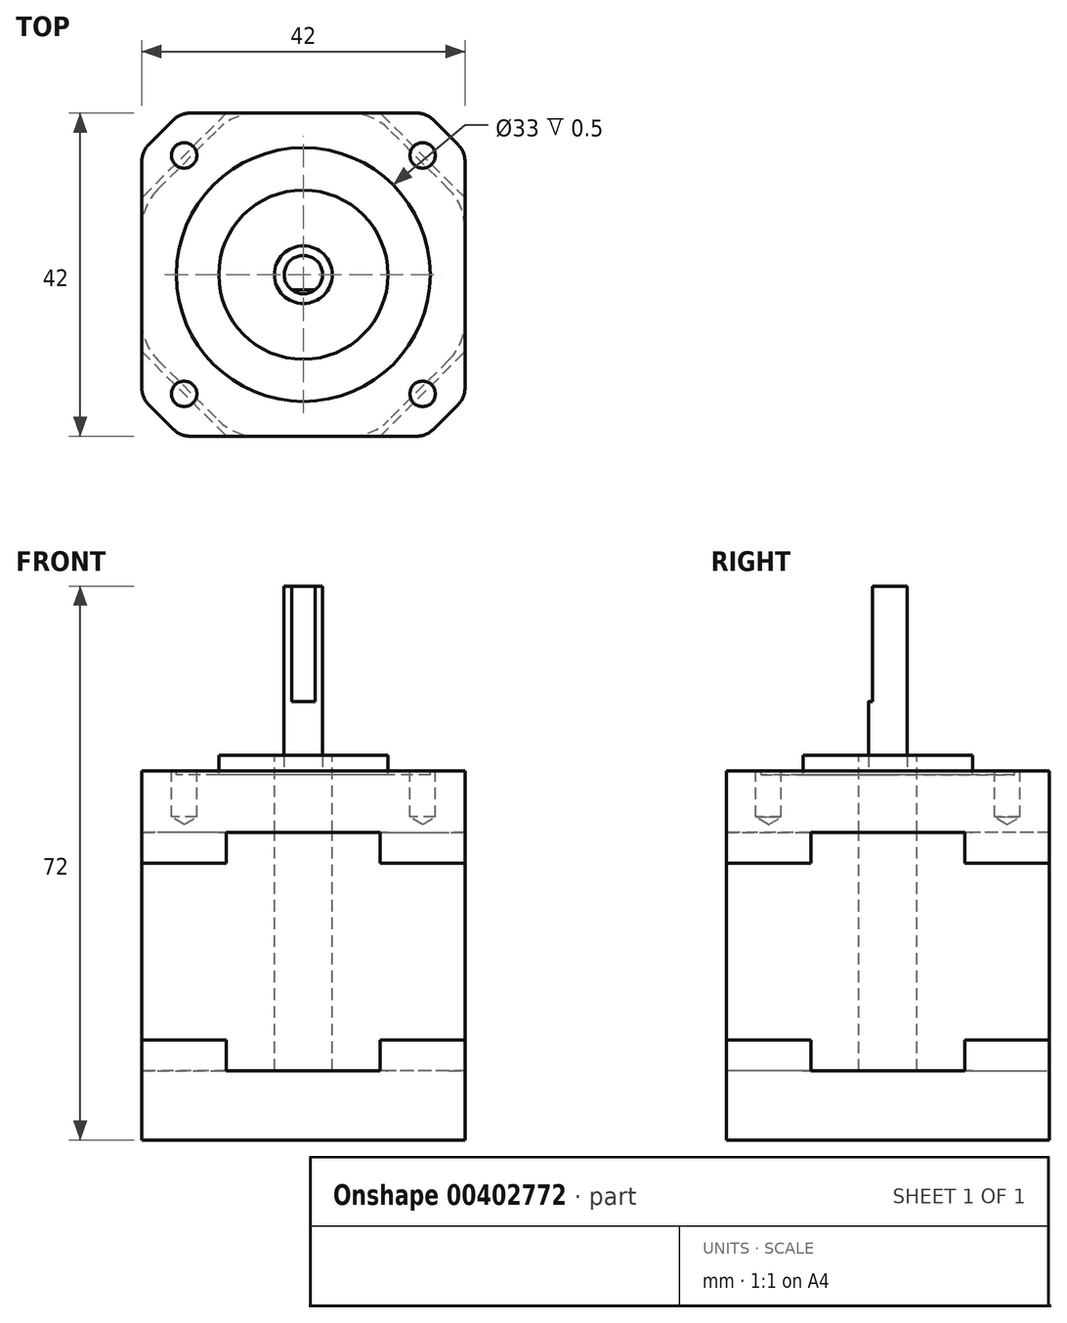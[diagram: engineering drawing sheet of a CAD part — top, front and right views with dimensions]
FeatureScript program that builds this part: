
annotation { "Feature Type Name" : "Feature", "Feature Type Description" : "" }
export const myFeature = defineFeature(function(context is Context, id is Id, definition is map)
    precondition{}
    {
        {
            var Q0;
            Q0=qCreatedBy(makeId("Top.planeOp"),FACE);
            var sketch = newSketch(context, id + "F0", { "sketchPlane" : qUnion([Q0])});
            skLineSegment(sketch, "E0.bottom", {"start": v(21, -21) * mm, "end": v(-21, -21) * mm});
            skLineSegment(sketch, "E0.top", {"start": v(21, 21) * mm, "end": v(-21, 21) * mm});
            skLineSegment(sketch, "E0.left", {"start": v(21, -21) * mm, "end": v(21, 21) * mm});
            skLineSegment(sketch, "E0.right", {"start": v(-21, -21) * mm, "end": v(-21, 21) * mm});
            skPoint(sketch, "E0.middle", {"position": v(0, 0) * mm});
            skCircle(sketch, "E1", {"center": v(0, 0) * mm, "radius": 3.75 * mm});
            skCircle(sketch, "E2", {"center": v(0, 0) * mm, "radius": 11 * mm});
            skCircle(sketch, "E3", {"center": v(0, 0) * mm, "radius": 16.5 * mm});
            skPoint(sketch, "E4", {"position": v(15.5, 15.5) * mm});
            skPoint(sketch, "E5.1.0", {"position": v(-15.5, 15.5) * mm});
            skPoint(sketch, "E5.2.0", {"position": v(-15.5, -15.5) * mm});
            skPoint(sketch, "E5.3.0", {"position": v(15.5, -15.5) * mm});
            skCircle(sketch, "E6", {"center": v(0, 0) * mm, "radius": 2.5 * mm});
            skSolve(sketch);
        }
        {
            var Q0;
            Q0=makeQuery(id+"F0.imprint","IMPRINT",FACE,{"disambiguationData":[TD([[makeQuery(id+"F0.imprint","IMPRINT",EDGE,{"derivedFrom":sQuery(id+"F0.wireOp",EDGE,"E0.bottom")}),-1.0]])]});
            var Q1;
            Q1=makeQuery(id+"F0.imprint","IMPRINT",FACE,{"disambiguationData":[TD([[makeQuery(id+"F0.imprint","IMPRINT",EDGE,{"derivedFrom":sQuery(id+"F0.wireOp",EDGE,"E2")}),-1.0]])]});
            var Q2;
            Q2=makeQuery(id+"F0.imprint","IMPRINT",FACE,{"disambiguationData":[TD([[makeQuery(id+"F0.imprint","IMPRINT",EDGE,{"derivedFrom":sQuery(id+"F0.wireOp",EDGE,"E1")}),-1.0]])]});
            extrude(context, id + "F1", {"entities" : qUnion([Q0, Q1, Q2]), "oppositeDirection" : true, "depth" : 8 * mm});
        }
        {
            var Q0;
            Q0=makeQuery(id+"F0.imprint","IMPRINT",FACE,{"disambiguationData":[TD([[makeQuery(id+"F0.imprint","IMPRINT",EDGE,{"derivedFrom":sQuery(id+"F0.wireOp",EDGE,"E2")}),-1.0]])]});
            extrude(context, id + "F2", {"entities" : qUnion([Q0]), "operationType" : NewBodyOperationType.REMOVE, "oppositeDirection" : true, "depth" : .5 * mm});
        }
        {
            var Q0;
            Q0=makeQuery(id+"F0.imprint","IMPRINT",FACE,{"disambiguationData":[TD([[makeQuery(id+"F0.imprint","IMPRINT",EDGE,{"derivedFrom":sQuery(id+"F0.wireOp",EDGE,"E1")}),-1.0]])]});
            extrude(context, id + "F3", {"entities" : qUnion([Q0]), "operationType" : NewBodyOperationType.ADD, "depth" : 2 * mm});
        }
        {
            var Q0;
            Q0=makeQuery(id+"F1.opExtrude","SWEPT_EDGE",EDGE,{"disambiguationData":[OSD([sQuery(id+"F0.wireOp",EDGE,"E0.bottom"),sQuery(id+"F0.wireOp",EDGE,"E0.left")])]});
            var Q1;
            Q1=makeQuery(id+"F1.opExtrude","SWEPT_EDGE",EDGE,{"disambiguationData":[OSD([sQuery(id+"F0.wireOp",EDGE,"E0.top"),sQuery(id+"F0.wireOp",EDGE,"E0.left")])]});
            var Q2;
            Q2=makeQuery(id+"F1.opExtrude","SWEPT_EDGE",EDGE,{"disambiguationData":[OSD([sQuery(id+"F0.wireOp",EDGE,"E0.bottom"),sQuery(id+"F0.wireOp",EDGE,"E0.right")])]});
            var Q3;
            Q3=makeQuery(id+"F1.opExtrude","SWEPT_EDGE",EDGE,{"disambiguationData":[OSD([sQuery(id+"F0.wireOp",EDGE,"E0.top"),sQuery(id+"F0.wireOp",EDGE,"E0.right")])]});
            chamfer(context, id + "F4", {"entities" : qUnion([Q0, Q1, Q2, Q3]), "width" : 5 * mm, "tangentPropagation" : true});
        }
        {
            var Q0;
            Q0=makeQuery(id+"F1.opExtrude","CAP_FACE",FACE,{"disambiguationData":[OSD([sQuery(id+"F0.wireOp",EDGE,"E0.bottom"),sQuery(id+"F0.wireOp",EDGE,"E0.top"),sQuery(id+"F0.wireOp",EDGE,"E0.left"),sQuery(id+"F0.wireOp",EDGE,"E0.right"),sQuery(id+"F0.wireOp",EDGE,"E1")])],"isStart":false});
            var sketch = newSketch(context, id + "F5", { "sketchPlane" : qUnion([Q0])});
            skLineSegment(sketch, "E7.bottom", {"start": v(-21, -21) * mm, "end": v(21, -21) * mm});
            skLineSegment(sketch, "E7.top", {"start": v(-21, 21) * mm, "end": v(21, 21) * mm});
            skLineSegment(sketch, "E7.left", {"start": v(-21, -21) * mm, "end": v(-21, 21) * mm});
            skLineSegment(sketch, "E7.right", {"start": v(21, -21) * mm, "end": v(21, 21) * mm});
            skPoint(sketch, "E7.middle", {"position": v(0, 0) * mm});
            skSolve(sketch);
        }
        {
            var Q0;
            {var subQ1=sQuery(id+"F0.wireOp",EDGE,"E1");Q0=makeQuery(id+"F5.imprint","IMPRINT",FACE,{"disambiguationData":[TD([[makeQuery(id+"F5.imprint","IMPRINT",EDGE,{"derivedFrom":makeQuery(id+"F1.opExtrude","CAP_EDGE",EDGE,{"disambiguationData":[OSD([subQ1])],"isStart":false})}),1.0]])]});}
            var Q1;
            {var subQ1=sQuery(id+"F0.wireOp",EDGE,"E0.left");var subQ2=sQuery(id+"F0.wireOp",EDGE,"E0.top");var subQ3=makeQuery(id+"F4.opChamfer","BLEND_EDGE",EDGE,{"blendedFrom":[makeQuery(id+"F1.opExtrude","SWEPT_EDGE",EDGE,{"disambiguationData":[OSD([subQ2,subQ1])]}),makeQuery(id+"F1.opExtrude","CAP_FACE",FACE,{"disambiguationData":[OSD([sQuery(id+"F0.wireOp",EDGE,"E0.bottom"),subQ2,subQ1,sQuery(id+"F0.wireOp",EDGE,"E0.right"),sQuery(id+"F0.wireOp",EDGE,"E1")])],"isStart":false})],"blendedInto":[makeQuery(id+"F1.opExtrude","CAP_FACE",FACE,{"disambiguationData":[OSD([sQuery(id+"F0.wireOp",EDGE,"E0.bottom"),subQ2,subQ1,sQuery(id+"F0.wireOp",EDGE,"E0.right"),sQuery(id+"F0.wireOp",EDGE,"E1")])],"isStart":false})]});Q1=makeQuery(id+"F5.imprint","IMPRINT",FACE,{"disambiguationData":[TD([[makeQuery(id+"F5.imprint","IMPRINT",EDGE,{"derivedFrom":subQ3}),-1.0]])]});}
            var Q2;
            {var subQ1=sQuery(id+"F0.wireOp",EDGE,"E0.right");var subQ2=sQuery(id+"F0.wireOp",EDGE,"E0.top");var subQ3=makeQuery(id+"F4.opChamfer","BLEND_EDGE",EDGE,{"blendedFrom":[makeQuery(id+"F1.opExtrude","SWEPT_EDGE",EDGE,{"disambiguationData":[OSD([subQ2,subQ1])]}),makeQuery(id+"F1.opExtrude","CAP_FACE",FACE,{"disambiguationData":[OSD([sQuery(id+"F0.wireOp",EDGE,"E0.bottom"),subQ2,sQuery(id+"F0.wireOp",EDGE,"E0.left"),subQ1,sQuery(id+"F0.wireOp",EDGE,"E1")])],"isStart":false})],"blendedInto":[makeQuery(id+"F1.opExtrude","CAP_FACE",FACE,{"disambiguationData":[OSD([sQuery(id+"F0.wireOp",EDGE,"E0.bottom"),subQ2,sQuery(id+"F0.wireOp",EDGE,"E0.left"),subQ1,sQuery(id+"F0.wireOp",EDGE,"E1")])],"isStart":false})]});Q2=makeQuery(id+"F5.imprint","IMPRINT",FACE,{"disambiguationData":[TD([[makeQuery(id+"F5.imprint","IMPRINT",EDGE,{"derivedFrom":subQ3}),-1.0]])]});}
            var Q3;
            {var subQ1=sQuery(id+"F0.wireOp",EDGE,"E0.right");var subQ2=sQuery(id+"F0.wireOp",EDGE,"E0.bottom");var subQ3=makeQuery(id+"F4.opChamfer","BLEND_EDGE",EDGE,{"blendedFrom":[makeQuery(id+"F1.opExtrude","SWEPT_EDGE",EDGE,{"disambiguationData":[OSD([subQ2,subQ1])]}),makeQuery(id+"F1.opExtrude","CAP_FACE",FACE,{"disambiguationData":[OSD([subQ2,sQuery(id+"F0.wireOp",EDGE,"E0.top"),sQuery(id+"F0.wireOp",EDGE,"E0.left"),subQ1,sQuery(id+"F0.wireOp",EDGE,"E1")])],"isStart":false})],"blendedInto":[makeQuery(id+"F1.opExtrude","CAP_FACE",FACE,{"disambiguationData":[OSD([subQ2,sQuery(id+"F0.wireOp",EDGE,"E0.top"),sQuery(id+"F0.wireOp",EDGE,"E0.left"),subQ1,sQuery(id+"F0.wireOp",EDGE,"E1")])],"isStart":false})]});Q3=makeQuery(id+"F5.imprint","IMPRINT",FACE,{"disambiguationData":[TD([[makeQuery(id+"F5.imprint","IMPRINT",EDGE,{"derivedFrom":subQ3}),-1.0]])]});}
            var Q4;
            {var subQ1=sQuery(id+"F0.wireOp",EDGE,"E0.left");var subQ2=sQuery(id+"F0.wireOp",EDGE,"E0.bottom");var subQ3=makeQuery(id+"F4.opChamfer","BLEND_EDGE",EDGE,{"blendedFrom":[makeQuery(id+"F1.opExtrude","SWEPT_EDGE",EDGE,{"disambiguationData":[OSD([subQ2,subQ1])]}),makeQuery(id+"F1.opExtrude","CAP_FACE",FACE,{"disambiguationData":[OSD([subQ2,sQuery(id+"F0.wireOp",EDGE,"E0.top"),subQ1,sQuery(id+"F0.wireOp",EDGE,"E0.right"),sQuery(id+"F0.wireOp",EDGE,"E1")])],"isStart":false})],"blendedInto":[makeQuery(id+"F1.opExtrude","CAP_FACE",FACE,{"disambiguationData":[OSD([subQ2,sQuery(id+"F0.wireOp",EDGE,"E0.top"),subQ1,sQuery(id+"F0.wireOp",EDGE,"E0.right"),sQuery(id+"F0.wireOp",EDGE,"E1")])],"isStart":false})]});Q4=makeQuery(id+"F5.imprint","IMPRINT",FACE,{"disambiguationData":[TD([[makeQuery(id+"F5.imprint","IMPRINT",EDGE,{"derivedFrom":subQ3}),-1.0]])]});}
            extrude(context, id + "F6", {"entities" : qUnion([Q0, Q1, Q2, Q3, Q4]), "depth" : 31 * mm});
        }
        {
            var Q0;
            Q0=makeQuery(id+"F6.opExtrude","SWEPT_EDGE",EDGE,{"disambiguationData":[OSD([sQuery(id+"F5.wireOp",EDGE,"E7.bottom"),sQuery(id+"F5.wireOp",EDGE,"E7.left")])]});
            var Q1;
            Q1=makeQuery(id+"F6.opExtrude","SWEPT_EDGE",EDGE,{"disambiguationData":[OSD([sQuery(id+"F5.wireOp",EDGE,"E7.bottom"),sQuery(id+"F5.wireOp",EDGE,"E7.right")])]});
            var Q2;
            Q2=makeQuery(id+"F6.opExtrude","SWEPT_EDGE",EDGE,{"disambiguationData":[OSD([sQuery(id+"F5.wireOp",EDGE,"E7.top"),sQuery(id+"F5.wireOp",EDGE,"E7.left")])]});
            var Q3;
            Q3=makeQuery(id+"F6.opExtrude","SWEPT_EDGE",EDGE,{"disambiguationData":[OSD([sQuery(id+"F5.wireOp",EDGE,"E7.top"),sQuery(id+"F5.wireOp",EDGE,"E7.right")])]});
            chamfer(context, id + "F7", {"entities" : qUnion([Q0, Q1, Q2, Q3]), "width" : 12 * mm, "tangentPropagation" : true});
        }
        {
            var Q0;
            Q0=makeQuery(id+"F6.opExtrude","CAP_FACE",FACE,{"disambiguationData":[OSD([sQuery(id+"F0.wireOp",EDGE,"E1"),sQuery(id+"F5.wireOp",EDGE,"E7.bottom"),sQuery(id+"F5.wireOp",EDGE,"E7.top"),sQuery(id+"F5.wireOp",EDGE,"E7.left"),sQuery(id+"F5.wireOp",EDGE,"E7.right")])],"isStart":false});
            var sketch = newSketch(context, id + "F8", { "sketchPlane" : qUnion([Q0])});
            skLineSegment(sketch, "E8.bottom", {"start": v(-21, -21) * mm, "end": v(21, -21) * mm});
            skLineSegment(sketch, "E8.top", {"start": v(-21, 21) * mm, "end": v(21, 21) * mm});
            skLineSegment(sketch, "E8.left", {"start": v(-21, -21) * mm, "end": v(-21, 21) * mm});
            skLineSegment(sketch, "E8.right", {"start": v(21, -21) * mm, "end": v(21, 21) * mm});
            skPoint(sketch, "E8.middle", {"position": v(0, 0) * mm});
            skSolve(sketch);
        }
        {
            var Q0;
            {var subQ1=sQuery(id+"F5.wireOp",EDGE,"E7.right");var subQ2=sQuery(id+"F5.wireOp",EDGE,"E7.bottom");var subQ3=makeQuery(id+"F7.opChamfer","BLEND_EDGE",EDGE,{"blendedFrom":[makeQuery(id+"F6.opExtrude","SWEPT_EDGE",EDGE,{"disambiguationData":[OSD([subQ2,subQ1])]}),makeQuery(id+"F6.opExtrude","CAP_FACE",FACE,{"disambiguationData":[OSD([sQuery(id+"F0.wireOp",EDGE,"E1"),subQ2,sQuery(id+"F5.wireOp",EDGE,"E7.top"),sQuery(id+"F5.wireOp",EDGE,"E7.left"),subQ1])],"isStart":false})],"blendedInto":[makeQuery(id+"F6.opExtrude","CAP_FACE",FACE,{"disambiguationData":[OSD([sQuery(id+"F0.wireOp",EDGE,"E1"),subQ2,sQuery(id+"F5.wireOp",EDGE,"E7.top"),sQuery(id+"F5.wireOp",EDGE,"E7.left"),subQ1])],"isStart":false})]});Q0=makeQuery(id+"F8.imprint","IMPRINT",FACE,{"disambiguationData":[TD([[makeQuery(id+"F8.imprint","IMPRINT",EDGE,{"derivedFrom":subQ3}),-1.0]])]});}
            var Q1;
            {var subQ1=sQuery(id+"F5.wireOp",EDGE,"E7.right");var subQ2=sQuery(id+"F5.wireOp",EDGE,"E7.top");var subQ3=makeQuery(id+"F7.opChamfer","BLEND_EDGE",EDGE,{"blendedFrom":[makeQuery(id+"F6.opExtrude","SWEPT_EDGE",EDGE,{"disambiguationData":[OSD([subQ2,subQ1])]}),makeQuery(id+"F6.opExtrude","CAP_FACE",FACE,{"disambiguationData":[OSD([sQuery(id+"F0.wireOp",EDGE,"E1"),sQuery(id+"F5.wireOp",EDGE,"E7.bottom"),subQ2,sQuery(id+"F5.wireOp",EDGE,"E7.left"),subQ1])],"isStart":false})],"blendedInto":[makeQuery(id+"F6.opExtrude","CAP_FACE",FACE,{"disambiguationData":[OSD([sQuery(id+"F0.wireOp",EDGE,"E1"),sQuery(id+"F5.wireOp",EDGE,"E7.bottom"),subQ2,sQuery(id+"F5.wireOp",EDGE,"E7.left"),subQ1])],"isStart":false})]});Q1=makeQuery(id+"F8.imprint","IMPRINT",FACE,{"disambiguationData":[TD([[makeQuery(id+"F8.imprint","IMPRINT",EDGE,{"derivedFrom":subQ3}),-1.0]])]});}
            var Q2;
            {var subQ1=sQuery(id+"F5.wireOp",EDGE,"E7.left");var subQ2=sQuery(id+"F5.wireOp",EDGE,"E7.top");var subQ3=makeQuery(id+"F7.opChamfer","BLEND_EDGE",EDGE,{"blendedFrom":[makeQuery(id+"F6.opExtrude","SWEPT_EDGE",EDGE,{"disambiguationData":[OSD([subQ2,subQ1])]}),makeQuery(id+"F6.opExtrude","CAP_FACE",FACE,{"disambiguationData":[OSD([sQuery(id+"F0.wireOp",EDGE,"E1"),sQuery(id+"F5.wireOp",EDGE,"E7.bottom"),subQ2,subQ1,sQuery(id+"F5.wireOp",EDGE,"E7.right")])],"isStart":false})],"blendedInto":[makeQuery(id+"F6.opExtrude","CAP_FACE",FACE,{"disambiguationData":[OSD([sQuery(id+"F0.wireOp",EDGE,"E1"),sQuery(id+"F5.wireOp",EDGE,"E7.bottom"),subQ2,subQ1,sQuery(id+"F5.wireOp",EDGE,"E7.right")])],"isStart":false})]});Q2=makeQuery(id+"F8.imprint","IMPRINT",FACE,{"disambiguationData":[TD([[makeQuery(id+"F8.imprint","IMPRINT",EDGE,{"derivedFrom":subQ3}),-1.0]])]});}
            var Q3;
            {var subQ1=sQuery(id+"F5.wireOp",EDGE,"E7.left");var subQ2=sQuery(id+"F5.wireOp",EDGE,"E7.bottom");var subQ3=makeQuery(id+"F7.opChamfer","BLEND_EDGE",EDGE,{"blendedFrom":[makeQuery(id+"F6.opExtrude","SWEPT_EDGE",EDGE,{"disambiguationData":[OSD([subQ2,subQ1])]}),makeQuery(id+"F6.opExtrude","CAP_FACE",FACE,{"disambiguationData":[OSD([sQuery(id+"F0.wireOp",EDGE,"E1"),subQ2,sQuery(id+"F5.wireOp",EDGE,"E7.top"),subQ1,sQuery(id+"F5.wireOp",EDGE,"E7.right")])],"isStart":false})],"blendedInto":[makeQuery(id+"F6.opExtrude","CAP_FACE",FACE,{"disambiguationData":[OSD([sQuery(id+"F0.wireOp",EDGE,"E1"),subQ2,sQuery(id+"F5.wireOp",EDGE,"E7.top"),subQ1,sQuery(id+"F5.wireOp",EDGE,"E7.right")])],"isStart":false})]});Q3=makeQuery(id+"F8.imprint","IMPRINT",FACE,{"disambiguationData":[TD([[makeQuery(id+"F8.imprint","IMPRINT",EDGE,{"derivedFrom":subQ3}),-1.0]])]});}
            var Q4;
            {var subQ5=sQuery(id+"F0.wireOp",EDGE,"E1");Q4=makeQuery(id+"F8.imprint","IMPRINT",FACE,{"disambiguationData":[TD([[makeQuery(id+"F8.imprint","IMPRINT",EDGE,{"derivedFrom":makeQuery(id+"F6.opExtrude","CAP_EDGE",EDGE,{"disambiguationData":[OSD([subQ5])],"isStart":false})}),1.0]])]});}
            var Q5;
            Q5=makeQuery(id+"F8.imprint","IMPRINT",FACE,{"disambiguationData":[TD([[makeQuery(id+"F8.imprint","IMPRINT",EDGE,{"derivedFrom":makeQuery(id+"F6.opExtrude","CAP_EDGE",EDGE,{"disambiguationData":[OSD([sQuery(id+"F0.wireOp",EDGE,"E1")])],"isStart":false})}),-1.0]])]});
            extrude(context, id + "F9", {"entities" : qUnion([Q0, Q1, Q2, Q3, Q4, Q5]), "depth" : 9 * mm});
        }
        {
            var Q0;
            Q0=makeQuery(id+"F9.opExtrude","SWEPT_EDGE",EDGE,{"disambiguationData":[OSD([sQuery(id+"F8.wireOp",EDGE,"E8.top"),sQuery(id+"F8.wireOp",EDGE,"E8.left")])]});
            var Q1;
            Q1=makeQuery(id+"F9.opExtrude","SWEPT_EDGE",EDGE,{"disambiguationData":[OSD([sQuery(id+"F8.wireOp",EDGE,"E8.bottom"),sQuery(id+"F8.wireOp",EDGE,"E8.left")])]});
            var Q2;
            Q2=makeQuery(id+"F9.opExtrude","SWEPT_EDGE",EDGE,{"disambiguationData":[OSD([sQuery(id+"F8.wireOp",EDGE,"E8.top"),sQuery(id+"F8.wireOp",EDGE,"E8.right")])]});
            var Q3;
            Q3=makeQuery(id+"F9.opExtrude","SWEPT_EDGE",EDGE,{"disambiguationData":[OSD([sQuery(id+"F8.wireOp",EDGE,"E8.bottom"),sQuery(id+"F8.wireOp",EDGE,"E8.right")])]});
            chamfer(context, id + "F10", {"entities" : qUnion([Q0, Q1, Q2, Q3]), "width" : 5 * mm, "tangentPropagation" : true});
        }
        {
            var Q0;
            Q0=sQuery(id+"F0.wireOp",VERTEX,"E5.1.0");
            var Q1;
            Q1=sQuery(id+"F0.wireOp",VERTEX,"E4");
            var Q2;
            Q2=sQuery(id+"F0.wireOp",VERTEX,"E5.3.0");
            var Q3;
            Q3=sQuery(id+"F0.wireOp",VERTEX,"E5.2.0");
            var Q4;
            Q4=makeQuery(id+"F1.opExtrude","SWEPT_BODY",BODY,{"disambiguationData":[OSD([sQuery(id+"F0.wireOp",EDGE,"E0.bottom"),sQuery(id+"F0.wireOp",EDGE,"E0.top"),sQuery(id+"F0.wireOp",EDGE,"E0.left"),sQuery(id+"F0.wireOp",EDGE,"E0.right"),sQuery(id+"F0.wireOp",EDGE,"E1")])]});
            hole(context, id + "F11", {"style" : HoleStyle.SIMPLE, "endStyle" : HoleEndStyle.BLIND, "standardTappedOrClearance" : lookupTablePath({ "fit" : "Normal", "standard" : "ISO", "engagement" : "75%", "pitch" : "0.5 mm", "size" : "M3", "type" : "Clearance & tapped" }), "standardBlindInLast" : lookupTablePath({ "standard" : "ISO", "fit" : "Standard", "engagement" : "75%", "pitch" : "0.5 mm", "size" : "M3", "type" : "Clearance & tapped" }), "holeDiameter" : 3.3 * mm, "showTappedDepth" : true, "holeDepth" : 6 * mm, "isTappedThrough" : true, "tappedDepth" : 4.5 * mm, "tapClearance" : 3, "locations" : qUnion([Q0, Q1, Q2, Q3]), "scope" : qUnion([Q4])});
        }
        {
            var Q0;
            Q0=makeQuery(id+"F9.opExtrude","CAP_FACE",FACE,{"disambiguationData":[OSD([sQuery(id+"F0.wireOp",EDGE,"E1"),sQuery(id+"F8.wireOp",EDGE,"E8.bottom"),sQuery(id+"F8.wireOp",EDGE,"E8.top"),sQuery(id+"F8.wireOp",EDGE,"E8.left"),sQuery(id+"F8.wireOp",EDGE,"E8.right")])],"isStart":true});
            var sketch = newSketch(context, id + "F12", { "sketchPlane" : qUnion([Q0])});
            skLineSegment(sketch, "E9", {"start": v(-21, 16) * mm, "end": v(-16, 21) * mm});
            skLineSegment(sketch, "E10", {"start": v(-16, 21) * mm, "end": v(-10, 21) * mm});
            skLineSegment(sketch, "E11", {"start": v(-10, 21) * mm, "end": v(-21, 10) * mm});
            skLineSegment(sketch, "E12", {"start": v(-21, 10) * mm, "end": v(-21, 16) * mm});
            skLineSegment(sketch, "E13.1.0", {"start": v(-21, -10) * mm, "end": v(-10, -21) * mm});
            skLineSegment(sketch, "E13.1.1", {"start": v(-16, -21) * mm, "end": v(-21, -16) * mm});
            skLineSegment(sketch, "E13.1.2", {"start": v(-21, -16) * mm, "end": v(-21, -10) * mm});
            skLineSegment(sketch, "E13.1.3", {"start": v(-10, -21) * mm, "end": v(-16, -21) * mm});
            skLineSegment(sketch, "E13.2.0", {"start": v(10, -21) * mm, "end": v(21, -10) * mm});
            skLineSegment(sketch, "E13.2.1", {"start": v(21, -16) * mm, "end": v(16, -21) * mm});
            skLineSegment(sketch, "E13.2.2", {"start": v(16, -21) * mm, "end": v(10, -21) * mm});
            skLineSegment(sketch, "E13.2.3", {"start": v(21, -10) * mm, "end": v(21, -16) * mm});
            skLineSegment(sketch, "E13.3.0", {"start": v(21, 10) * mm, "end": v(10, 21) * mm});
            skLineSegment(sketch, "E13.3.1", {"start": v(16, 21) * mm, "end": v(21, 16) * mm});
            skLineSegment(sketch, "E13.3.2", {"start": v(21, 16) * mm, "end": v(21, 10) * mm});
            skLineSegment(sketch, "E13.3.3", {"start": v(10, 21) * mm, "end": v(16, 21) * mm});
            skPoint(sketch, "E13.center", {"position": v(0, 0) * mm});
            skSolve(sketch);
        }
        {
            var Q0;
            Q0=makeQuery(id+"F12.imprint","IMPRINT",FACE,{"disambiguationData":[TD([[makeQuery(id+"F12.imprint","IMPRINT",EDGE,{"derivedFrom":sQuery(id+"F12.wireOp",EDGE,"E9")}),1.0]])]});
            var Q1;
            Q1=makeQuery(id+"F12.imprint","IMPRINT",FACE,{"disambiguationData":[TD([[makeQuery(id+"F12.imprint","IMPRINT",EDGE,{"derivedFrom":sQuery(id+"F12.wireOp",EDGE,"E13.1.0")}),-1.0]])]});
            var Q2;
            Q2=makeQuery(id+"F12.imprint","IMPRINT",FACE,{"disambiguationData":[TD([[makeQuery(id+"F12.imprint","IMPRINT",EDGE,{"derivedFrom":sQuery(id+"F12.wireOp",EDGE,"E13.2.0")}),-1.0]])]});
            var Q3;
            Q3=makeQuery(id+"F12.imprint","IMPRINT",FACE,{"disambiguationData":[TD([[makeQuery(id+"F12.imprint","IMPRINT",EDGE,{"derivedFrom":sQuery(id+"F12.wireOp",EDGE,"E13.3.0")}),-1.0]])]});
            extrude(context, id + "F13", {"entities" : qUnion([Q0, Q1, Q2, Q3]), "operationType" : NewBodyOperationType.ADD, "depth" : 4 * mm});
        }
        {
            var Q0;
            Q0=makeQuery(id+"F1.opExtrude","CAP_FACE",FACE,{"disambiguationData":[OSD([sQuery(id+"F0.wireOp",EDGE,"E0.bottom"),sQuery(id+"F0.wireOp",EDGE,"E0.top"),sQuery(id+"F0.wireOp",EDGE,"E0.left"),sQuery(id+"F0.wireOp",EDGE,"E0.right"),sQuery(id+"F0.wireOp",EDGE,"E1")])],"isStart":false});
            var sketch = newSketch(context, id + "F14", { "sketchPlane" : qUnion([Q0])});
            skLineSegment(sketch, "E14", {"start": v(16, 21) * mm, "end": v(21, 16) * mm});
            skLineSegment(sketch, "E15", {"start": v(21, 16) * mm, "end": v(21, 10) * mm});
            skLineSegment(sketch, "E16", {"start": v(21, 10) * mm, "end": v(10, 21) * mm});
            skLineSegment(sketch, "E17", {"start": v(10, 21) * mm, "end": v(16, 21) * mm});
            skLineSegment(sketch, "E18.1.0", {"start": v(-10, 21) * mm, "end": v(-21, 10) * mm});
            skLineSegment(sketch, "E18.1.1", {"start": v(-21, 10) * mm, "end": v(-21, 16) * mm});
            skLineSegment(sketch, "E18.1.2", {"start": v(-16, 21) * mm, "end": v(-10, 21) * mm});
            skLineSegment(sketch, "E18.1.3", {"start": v(-21, 16) * mm, "end": v(-16, 21) * mm});
            skLineSegment(sketch, "E18.2.0", {"start": v(-21, -10) * mm, "end": v(-10, -21) * mm});
            skLineSegment(sketch, "E18.2.1", {"start": v(-10, -21) * mm, "end": v(-16, -21) * mm});
            skLineSegment(sketch, "E18.2.2", {"start": v(-21, -16) * mm, "end": v(-21, -10) * mm});
            skLineSegment(sketch, "E18.2.3", {"start": v(-16, -21) * mm, "end": v(-21, -16) * mm});
            skLineSegment(sketch, "E18.3.0", {"start": v(10, -21) * mm, "end": v(21, -10) * mm});
            skLineSegment(sketch, "E18.3.1", {"start": v(21, -10) * mm, "end": v(21, -16) * mm});
            skLineSegment(sketch, "E18.3.2", {"start": v(16, -21) * mm, "end": v(10, -21) * mm});
            skLineSegment(sketch, "E18.3.3", {"start": v(21, -16) * mm, "end": v(16, -21) * mm});
            skPoint(sketch, "E18.center", {"position": v(0, 0) * mm});
            skSolve(sketch);
        }
        {
            var Q0;
            Q0=makeQuery(id+"F14.imprint","IMPRINT",FACE,{"disambiguationData":[TD([[makeQuery(id+"F14.imprint","IMPRINT",EDGE,{"derivedFrom":sQuery(id+"F14.wireOp",EDGE,"E14")}),1.0]])]});
            var Q1;
            Q1=makeQuery(id+"F14.imprint","IMPRINT",FACE,{"disambiguationData":[TD([[makeQuery(id+"F14.imprint","IMPRINT",EDGE,{"derivedFrom":sQuery(id+"F14.wireOp",EDGE,"E18.1.0")}),-1.0]])]});
            var Q2;
            Q2=makeQuery(id+"F14.imprint","IMPRINT",FACE,{"disambiguationData":[TD([[makeQuery(id+"F14.imprint","IMPRINT",EDGE,{"derivedFrom":sQuery(id+"F14.wireOp",EDGE,"E18.2.0")}),-1.0]])]});
            var Q3;
            Q3=makeQuery(id+"F14.imprint","IMPRINT",FACE,{"disambiguationData":[TD([[makeQuery(id+"F14.imprint","IMPRINT",EDGE,{"derivedFrom":sQuery(id+"F14.wireOp",EDGE,"E18.3.0")}),-1.0]])]});
            extrude(context, id + "F15", {"entities" : qUnion([Q0, Q1, Q2, Q3]), "operationType" : NewBodyOperationType.ADD, "depth" : 4 * mm});
        }
        {
            var Q0;
            {var subQ0=sQuery(id+"F8.wireOp",EDGE,"E8.right");Q0=makeQuery(id+"F13.boolean.opBoolean","MERGE",EDGE,{"derivedFrom":[makeQuery(id+"F10.opChamfer","BLEND_EDGE",EDGE,{"blendedFrom":[makeQuery(id+"F9.opExtrude","SWEPT_EDGE",EDGE,{"disambiguationData":[OSD([sQuery(id+"F8.wireOp",EDGE,"E8.top"),subQ0])]}),makeQuery(id+"F9.opExtrude","SWEPT_FACE",FACE,{"disambiguationData":[OSD([subQ0])]})],"blendedInto":[makeQuery(id+"F9.opExtrude","SWEPT_FACE",FACE,{"disambiguationData":[OSD([subQ0])]})]}),makeQuery(id+"F13.opExtrude","SWEPT_EDGE",EDGE,{"disambiguationData":[OSD([sQuery(id+"F12.wireOp",EDGE,"E13.2.1"),sQuery(id+"F12.wireOp",EDGE,"E13.2.3")])]})]});}
            var Q1;
            {var subQ0=sQuery(id+"F8.wireOp",EDGE,"E8.top");Q1=makeQuery(id+"F13.boolean.opBoolean","MERGE",EDGE,{"derivedFrom":[makeQuery(id+"F10.opChamfer","BLEND_EDGE",EDGE,{"blendedFrom":[makeQuery(id+"F9.opExtrude","SWEPT_EDGE",EDGE,{"disambiguationData":[OSD([subQ0,sQuery(id+"F8.wireOp",EDGE,"E8.right")])]}),makeQuery(id+"F9.opExtrude","SWEPT_FACE",FACE,{"disambiguationData":[OSD([subQ0])]})],"blendedInto":[makeQuery(id+"F9.opExtrude","SWEPT_FACE",FACE,{"disambiguationData":[OSD([subQ0])]})]}),makeQuery(id+"F13.opExtrude","SWEPT_EDGE",EDGE,{"disambiguationData":[OSD([sQuery(id+"F12.wireOp",EDGE,"E13.2.1"),sQuery(id+"F12.wireOp",EDGE,"E13.2.2")])]})]});}
            var Q2;
            {var subQ0=sQuery(id+"F8.wireOp",EDGE,"E8.right");Q2=makeQuery(id+"F13.boolean.opBoolean","MERGE",EDGE,{"derivedFrom":[makeQuery(id+"F10.opChamfer","BLEND_EDGE",EDGE,{"blendedFrom":[makeQuery(id+"F9.opExtrude","SWEPT_EDGE",EDGE,{"disambiguationData":[OSD([sQuery(id+"F8.wireOp",EDGE,"E8.bottom"),subQ0])]}),makeQuery(id+"F9.opExtrude","SWEPT_FACE",FACE,{"disambiguationData":[OSD([subQ0])]})],"blendedInto":[makeQuery(id+"F9.opExtrude","SWEPT_FACE",FACE,{"disambiguationData":[OSD([subQ0])]})]}),makeQuery(id+"F13.opExtrude","SWEPT_EDGE",EDGE,{"disambiguationData":[OSD([sQuery(id+"F12.wireOp",EDGE,"E13.3.1"),sQuery(id+"F12.wireOp",EDGE,"E13.3.2")])]})]});}
            var Q3;
            {var subQ0=sQuery(id+"F8.wireOp",EDGE,"E8.bottom");Q3=makeQuery(id+"F13.boolean.opBoolean","MERGE",EDGE,{"derivedFrom":[makeQuery(id+"F10.opChamfer","BLEND_EDGE",EDGE,{"blendedFrom":[makeQuery(id+"F9.opExtrude","SWEPT_EDGE",EDGE,{"disambiguationData":[OSD([subQ0,sQuery(id+"F8.wireOp",EDGE,"E8.right")])]}),makeQuery(id+"F9.opExtrude","SWEPT_FACE",FACE,{"disambiguationData":[OSD([subQ0])]})],"blendedInto":[makeQuery(id+"F9.opExtrude","SWEPT_FACE",FACE,{"disambiguationData":[OSD([subQ0])]})]}),makeQuery(id+"F13.opExtrude","SWEPT_EDGE",EDGE,{"disambiguationData":[OSD([sQuery(id+"F12.wireOp",EDGE,"E13.3.1"),sQuery(id+"F12.wireOp",EDGE,"E13.3.3")])]})]});}
            var Q4;
            {var subQ0=sQuery(id+"F8.wireOp",EDGE,"E8.bottom");Q4=makeQuery(id+"F13.boolean.opBoolean","MERGE",EDGE,{"derivedFrom":[makeQuery(id+"F10.opChamfer","BLEND_EDGE",EDGE,{"blendedFrom":[makeQuery(id+"F9.opExtrude","SWEPT_EDGE",EDGE,{"disambiguationData":[OSD([subQ0,sQuery(id+"F8.wireOp",EDGE,"E8.left")])]}),makeQuery(id+"F9.opExtrude","SWEPT_FACE",FACE,{"disambiguationData":[OSD([subQ0])]})],"blendedInto":[makeQuery(id+"F9.opExtrude","SWEPT_FACE",FACE,{"disambiguationData":[OSD([subQ0])]})]}),makeQuery(id+"F13.opExtrude","SWEPT_EDGE",EDGE,{"disambiguationData":[OSD([sQuery(id+"F12.wireOp",EDGE,"E9"),sQuery(id+"F12.wireOp",EDGE,"E10")])]})]});}
            var Q5;
            {var subQ0=sQuery(id+"F8.wireOp",EDGE,"E8.left");Q5=makeQuery(id+"F13.boolean.opBoolean","MERGE",EDGE,{"derivedFrom":[makeQuery(id+"F10.opChamfer","BLEND_EDGE",EDGE,{"blendedFrom":[makeQuery(id+"F9.opExtrude","SWEPT_EDGE",EDGE,{"disambiguationData":[OSD([sQuery(id+"F8.wireOp",EDGE,"E8.bottom"),subQ0])]}),makeQuery(id+"F9.opExtrude","SWEPT_FACE",FACE,{"disambiguationData":[OSD([subQ0])]})],"blendedInto":[makeQuery(id+"F9.opExtrude","SWEPT_FACE",FACE,{"disambiguationData":[OSD([subQ0])]})]}),makeQuery(id+"F13.opExtrude","SWEPT_EDGE",EDGE,{"disambiguationData":[OSD([sQuery(id+"F12.wireOp",EDGE,"E9"),sQuery(id+"F12.wireOp",EDGE,"E12")])]})]});}
            var Q6;
            {var subQ0=sQuery(id+"F8.wireOp",EDGE,"E8.left");Q6=makeQuery(id+"F13.boolean.opBoolean","MERGE",EDGE,{"derivedFrom":[makeQuery(id+"F10.opChamfer","BLEND_EDGE",EDGE,{"blendedFrom":[makeQuery(id+"F9.opExtrude","SWEPT_EDGE",EDGE,{"disambiguationData":[OSD([sQuery(id+"F8.wireOp",EDGE,"E8.top"),subQ0])]}),makeQuery(id+"F9.opExtrude","SWEPT_FACE",FACE,{"disambiguationData":[OSD([subQ0])]})],"blendedInto":[makeQuery(id+"F9.opExtrude","SWEPT_FACE",FACE,{"disambiguationData":[OSD([subQ0])]})]}),makeQuery(id+"F13.opExtrude","SWEPT_EDGE",EDGE,{"disambiguationData":[OSD([sQuery(id+"F12.wireOp",EDGE,"E13.1.1"),sQuery(id+"F12.wireOp",EDGE,"E13.1.2")])]})]});}
            var Q7;
            {var subQ0=sQuery(id+"F8.wireOp",EDGE,"E8.top");Q7=makeQuery(id+"F13.boolean.opBoolean","MERGE",EDGE,{"derivedFrom":[makeQuery(id+"F10.opChamfer","BLEND_EDGE",EDGE,{"blendedFrom":[makeQuery(id+"F9.opExtrude","SWEPT_EDGE",EDGE,{"disambiguationData":[OSD([subQ0,sQuery(id+"F8.wireOp",EDGE,"E8.left")])]}),makeQuery(id+"F9.opExtrude","SWEPT_FACE",FACE,{"disambiguationData":[OSD([subQ0])]})],"blendedInto":[makeQuery(id+"F9.opExtrude","SWEPT_FACE",FACE,{"disambiguationData":[OSD([subQ0])]})]}),makeQuery(id+"F13.opExtrude","SWEPT_EDGE",EDGE,{"disambiguationData":[OSD([sQuery(id+"F12.wireOp",EDGE,"E13.1.1"),sQuery(id+"F12.wireOp",EDGE,"E13.1.3")])]})]});}
            var Q8;
            {var subQ0=sQuery(id+"F0.wireOp",EDGE,"E0.bottom");Q8=makeQuery(id+"F15.boolean.opBoolean","MERGE",EDGE,{"derivedFrom":[makeQuery(id+"F4.opChamfer","BLEND_EDGE",EDGE,{"blendedFrom":[makeQuery(id+"F1.opExtrude","SWEPT_EDGE",EDGE,{"disambiguationData":[OSD([subQ0,sQuery(id+"F0.wireOp",EDGE,"E0.right")])]}),makeQuery(id+"F1.opExtrude","SWEPT_FACE",FACE,{"disambiguationData":[OSD([subQ0])]})],"blendedInto":[makeQuery(id+"F1.opExtrude","SWEPT_FACE",FACE,{"disambiguationData":[OSD([subQ0])]})]}),makeQuery(id+"F15.opExtrude","SWEPT_EDGE",EDGE,{"disambiguationData":[OSD([sQuery(id+"F14.wireOp",EDGE,"E18.1.2"),sQuery(id+"F14.wireOp",EDGE,"E18.1.3")])]})]});}
            var Q9;
            {var subQ0=sQuery(id+"F0.wireOp",EDGE,"E0.right");Q9=makeQuery(id+"F15.boolean.opBoolean","MERGE",EDGE,{"derivedFrom":[makeQuery(id+"F4.opChamfer","BLEND_EDGE",EDGE,{"blendedFrom":[makeQuery(id+"F1.opExtrude","SWEPT_EDGE",EDGE,{"disambiguationData":[OSD([sQuery(id+"F0.wireOp",EDGE,"E0.bottom"),subQ0])]}),makeQuery(id+"F1.opExtrude","SWEPT_FACE",FACE,{"disambiguationData":[OSD([subQ0])]})],"blendedInto":[makeQuery(id+"F1.opExtrude","SWEPT_FACE",FACE,{"disambiguationData":[OSD([subQ0])]})]}),makeQuery(id+"F15.opExtrude","SWEPT_EDGE",EDGE,{"disambiguationData":[OSD([sQuery(id+"F14.wireOp",EDGE,"E18.1.1"),sQuery(id+"F14.wireOp",EDGE,"E18.1.3")])]})]});}
            var Q10;
            {var subQ0=sQuery(id+"F0.wireOp",EDGE,"E0.right");Q10=makeQuery(id+"F15.boolean.opBoolean","MERGE",EDGE,{"derivedFrom":[makeQuery(id+"F4.opChamfer","BLEND_EDGE",EDGE,{"blendedFrom":[makeQuery(id+"F1.opExtrude","SWEPT_EDGE",EDGE,{"disambiguationData":[OSD([sQuery(id+"F0.wireOp",EDGE,"E0.top"),subQ0])]}),makeQuery(id+"F1.opExtrude","SWEPT_FACE",FACE,{"disambiguationData":[OSD([subQ0])]})],"blendedInto":[makeQuery(id+"F1.opExtrude","SWEPT_FACE",FACE,{"disambiguationData":[OSD([subQ0])]})]}),makeQuery(id+"F15.opExtrude","SWEPT_EDGE",EDGE,{"disambiguationData":[OSD([sQuery(id+"F14.wireOp",EDGE,"E18.2.2"),sQuery(id+"F14.wireOp",EDGE,"E18.2.3")])]})]});}
            var Q11;
            {var subQ0=sQuery(id+"F0.wireOp",EDGE,"E0.top");Q11=makeQuery(id+"F15.boolean.opBoolean","MERGE",EDGE,{"derivedFrom":[makeQuery(id+"F4.opChamfer","BLEND_EDGE",EDGE,{"blendedFrom":[makeQuery(id+"F1.opExtrude","SWEPT_EDGE",EDGE,{"disambiguationData":[OSD([subQ0,sQuery(id+"F0.wireOp",EDGE,"E0.right")])]}),makeQuery(id+"F1.opExtrude","SWEPT_FACE",FACE,{"disambiguationData":[OSD([subQ0])]})],"blendedInto":[makeQuery(id+"F1.opExtrude","SWEPT_FACE",FACE,{"disambiguationData":[OSD([subQ0])]})]}),makeQuery(id+"F15.opExtrude","SWEPT_EDGE",EDGE,{"disambiguationData":[OSD([sQuery(id+"F14.wireOp",EDGE,"E18.2.1"),sQuery(id+"F14.wireOp",EDGE,"E18.2.3")])]})]});}
            var Q12;
            {var subQ0=sQuery(id+"F0.wireOp",EDGE,"E0.top");Q12=makeQuery(id+"F15.boolean.opBoolean","MERGE",EDGE,{"derivedFrom":[makeQuery(id+"F4.opChamfer","BLEND_EDGE",EDGE,{"blendedFrom":[makeQuery(id+"F1.opExtrude","SWEPT_EDGE",EDGE,{"disambiguationData":[OSD([subQ0,sQuery(id+"F0.wireOp",EDGE,"E0.left")])]}),makeQuery(id+"F1.opExtrude","SWEPT_FACE",FACE,{"disambiguationData":[OSD([subQ0])]})],"blendedInto":[makeQuery(id+"F1.opExtrude","SWEPT_FACE",FACE,{"disambiguationData":[OSD([subQ0])]})]}),makeQuery(id+"F15.opExtrude","SWEPT_EDGE",EDGE,{"disambiguationData":[OSD([sQuery(id+"F14.wireOp",EDGE,"E18.3.2"),sQuery(id+"F14.wireOp",EDGE,"E18.3.3")])]})]});}
            var Q13;
            {var subQ0=sQuery(id+"F0.wireOp",EDGE,"E0.left");Q13=makeQuery(id+"F15.boolean.opBoolean","MERGE",EDGE,{"derivedFrom":[makeQuery(id+"F4.opChamfer","BLEND_EDGE",EDGE,{"blendedFrom":[makeQuery(id+"F1.opExtrude","SWEPT_EDGE",EDGE,{"disambiguationData":[OSD([sQuery(id+"F0.wireOp",EDGE,"E0.top"),subQ0])]}),makeQuery(id+"F1.opExtrude","SWEPT_FACE",FACE,{"disambiguationData":[OSD([subQ0])]})],"blendedInto":[makeQuery(id+"F1.opExtrude","SWEPT_FACE",FACE,{"disambiguationData":[OSD([subQ0])]})]}),makeQuery(id+"F15.opExtrude","SWEPT_EDGE",EDGE,{"disambiguationData":[OSD([sQuery(id+"F14.wireOp",EDGE,"E18.3.1"),sQuery(id+"F14.wireOp",EDGE,"E18.3.3")])]})]});}
            var Q14;
            {var subQ0=sQuery(id+"F0.wireOp",EDGE,"E0.left");Q14=makeQuery(id+"F15.boolean.opBoolean","MERGE",EDGE,{"derivedFrom":[makeQuery(id+"F4.opChamfer","BLEND_EDGE",EDGE,{"blendedFrom":[makeQuery(id+"F1.opExtrude","SWEPT_EDGE",EDGE,{"disambiguationData":[OSD([sQuery(id+"F0.wireOp",EDGE,"E0.bottom"),subQ0])]}),makeQuery(id+"F1.opExtrude","SWEPT_FACE",FACE,{"disambiguationData":[OSD([subQ0])]})],"blendedInto":[makeQuery(id+"F1.opExtrude","SWEPT_FACE",FACE,{"disambiguationData":[OSD([subQ0])]})]}),makeQuery(id+"F15.opExtrude","SWEPT_EDGE",EDGE,{"disambiguationData":[OSD([sQuery(id+"F14.wireOp",EDGE,"E14"),sQuery(id+"F14.wireOp",EDGE,"E15")])]})]});}
            var Q15;
            {var subQ0=sQuery(id+"F0.wireOp",EDGE,"E0.bottom");Q15=makeQuery(id+"F15.boolean.opBoolean","MERGE",EDGE,{"derivedFrom":[makeQuery(id+"F4.opChamfer","BLEND_EDGE",EDGE,{"blendedFrom":[makeQuery(id+"F1.opExtrude","SWEPT_EDGE",EDGE,{"disambiguationData":[OSD([subQ0,sQuery(id+"F0.wireOp",EDGE,"E0.left")])]}),makeQuery(id+"F1.opExtrude","SWEPT_FACE",FACE,{"disambiguationData":[OSD([subQ0])]})],"blendedInto":[makeQuery(id+"F1.opExtrude","SWEPT_FACE",FACE,{"disambiguationData":[OSD([subQ0])]})]}),makeQuery(id+"F15.opExtrude","SWEPT_EDGE",EDGE,{"disambiguationData":[OSD([sQuery(id+"F14.wireOp",EDGE,"E14"),sQuery(id+"F14.wireOp",EDGE,"E17")])]})]});}
            fillet(context, id + "F16", {"entities" : qUnion([Q0, Q1, Q2, Q3, Q4, Q5, Q6, Q7, Q8, Q9, Q10, Q11, Q12, Q13, Q14, Q15]), "radius" : 3 * mm, "tangentPropagation" : true, "allowEdgeOverflow" : false});
        }
        {
            var Q0;
            {var subQ0=sQuery(id+"F5.wireOp",EDGE,"E7.top");Q0=makeQuery(id+"F7.opChamfer","BLEND_EDGE",EDGE,{"blendedFrom":[makeQuery(id+"F6.opExtrude","SWEPT_EDGE",EDGE,{"disambiguationData":[OSD([subQ0,sQuery(id+"F5.wireOp",EDGE,"E7.left")])]}),makeQuery(id+"F6.opExtrude","SWEPT_FACE",FACE,{"disambiguationData":[OSD([subQ0])]})],"blendedInto":[makeQuery(id+"F6.opExtrude","SWEPT_FACE",FACE,{"disambiguationData":[OSD([subQ0])]})]});}
            var Q1;
            {var subQ0=sQuery(id+"F5.wireOp",EDGE,"E7.left");Q1=makeQuery(id+"F7.opChamfer","BLEND_EDGE",EDGE,{"blendedFrom":[makeQuery(id+"F6.opExtrude","SWEPT_EDGE",EDGE,{"disambiguationData":[OSD([sQuery(id+"F5.wireOp",EDGE,"E7.top"),subQ0])]}),makeQuery(id+"F6.opExtrude","SWEPT_FACE",FACE,{"disambiguationData":[OSD([subQ0])]})],"blendedInto":[makeQuery(id+"F6.opExtrude","SWEPT_FACE",FACE,{"disambiguationData":[OSD([subQ0])]})]});}
            var Q2;
            {var subQ0=sQuery(id+"F5.wireOp",EDGE,"E7.top");Q2=makeQuery(id+"F7.opChamfer","BLEND_EDGE",EDGE,{"blendedFrom":[makeQuery(id+"F6.opExtrude","SWEPT_EDGE",EDGE,{"disambiguationData":[OSD([subQ0,sQuery(id+"F5.wireOp",EDGE,"E7.right")])]}),makeQuery(id+"F6.opExtrude","SWEPT_FACE",FACE,{"disambiguationData":[OSD([subQ0])]})],"blendedInto":[makeQuery(id+"F6.opExtrude","SWEPT_FACE",FACE,{"disambiguationData":[OSD([subQ0])]})]});}
            var Q3;
            {var subQ0=sQuery(id+"F5.wireOp",EDGE,"E7.right");Q3=makeQuery(id+"F7.opChamfer","BLEND_EDGE",EDGE,{"blendedFrom":[makeQuery(id+"F6.opExtrude","SWEPT_EDGE",EDGE,{"disambiguationData":[OSD([sQuery(id+"F5.wireOp",EDGE,"E7.top"),subQ0])]}),makeQuery(id+"F6.opExtrude","SWEPT_FACE",FACE,{"disambiguationData":[OSD([subQ0])]})],"blendedInto":[makeQuery(id+"F6.opExtrude","SWEPT_FACE",FACE,{"disambiguationData":[OSD([subQ0])]})]});}
            var Q4;
            {var subQ0=sQuery(id+"F5.wireOp",EDGE,"E7.right");Q4=makeQuery(id+"F7.opChamfer","BLEND_EDGE",EDGE,{"blendedFrom":[makeQuery(id+"F6.opExtrude","SWEPT_EDGE",EDGE,{"disambiguationData":[OSD([sQuery(id+"F5.wireOp",EDGE,"E7.bottom"),subQ0])]}),makeQuery(id+"F6.opExtrude","SWEPT_FACE",FACE,{"disambiguationData":[OSD([subQ0])]})],"blendedInto":[makeQuery(id+"F6.opExtrude","SWEPT_FACE",FACE,{"disambiguationData":[OSD([subQ0])]})]});}
            var Q5;
            {var subQ0=sQuery(id+"F5.wireOp",EDGE,"E7.bottom");Q5=makeQuery(id+"F7.opChamfer","BLEND_EDGE",EDGE,{"blendedFrom":[makeQuery(id+"F6.opExtrude","SWEPT_EDGE",EDGE,{"disambiguationData":[OSD([subQ0,sQuery(id+"F5.wireOp",EDGE,"E7.right")])]}),makeQuery(id+"F6.opExtrude","SWEPT_FACE",FACE,{"disambiguationData":[OSD([subQ0])]})],"blendedInto":[makeQuery(id+"F6.opExtrude","SWEPT_FACE",FACE,{"disambiguationData":[OSD([subQ0])]})]});}
            var Q6;
            {var subQ0=sQuery(id+"F5.wireOp",EDGE,"E7.bottom");Q6=makeQuery(id+"F7.opChamfer","BLEND_EDGE",EDGE,{"blendedFrom":[makeQuery(id+"F6.opExtrude","SWEPT_EDGE",EDGE,{"disambiguationData":[OSD([subQ0,sQuery(id+"F5.wireOp",EDGE,"E7.left")])]}),makeQuery(id+"F6.opExtrude","SWEPT_FACE",FACE,{"disambiguationData":[OSD([subQ0])]})],"blendedInto":[makeQuery(id+"F6.opExtrude","SWEPT_FACE",FACE,{"disambiguationData":[OSD([subQ0])]})]});}
            var Q7;
            {var subQ0=sQuery(id+"F5.wireOp",EDGE,"E7.left");Q7=makeQuery(id+"F7.opChamfer","BLEND_EDGE",EDGE,{"blendedFrom":[makeQuery(id+"F6.opExtrude","SWEPT_EDGE",EDGE,{"disambiguationData":[OSD([sQuery(id+"F5.wireOp",EDGE,"E7.bottom"),subQ0])]}),makeQuery(id+"F6.opExtrude","SWEPT_FACE",FACE,{"disambiguationData":[OSD([subQ0])]})],"blendedInto":[makeQuery(id+"F6.opExtrude","SWEPT_FACE",FACE,{"disambiguationData":[OSD([subQ0])]})]});}
            fillet(context, id + "F17", {"entities" : qUnion([Q0, Q1, Q2, Q3, Q4, Q5, Q6, Q7]), "radius" : 7 * mm, "tangentPropagation" : true, "allowEdgeOverflow" : false});
        }
        {
            var Q0;
            Q0=makeQuery(id+"F0.imprint","IMPRINT",FACE,{"disambiguationData":[TD([[makeQuery(id+"F0.imprint","IMPRINT",EDGE,{"derivedFrom":sQuery(id+"F0.wireOp",EDGE,"E6")}),1.0]])]});
            extrude(context, id + "F18", {"entities" : qUnion([Q0]), "depth" : 24 * mm});
        }
        {
            var Q0;
            Q0=makeQuery(id+"F18.opExtrude","CAP_FACE",FACE,{"disambiguationData":[OSD([sQuery(id+"F0.wireOp",EDGE,"E6")])],"isStart":false});
            var sketch = newSketch(context, id + "F19", { "sketchPlane" : qUnion([Q0])});
            skLineSegment(sketch, "E19", {"start": v(-1.5, -2) * mm, "end": v(1.5, -2) * mm});
            skSolve(sketch);
        }
        {
            var Q0;
            {var subQ0=sQuery(id+"F19.wireOp",EDGE,"E19");Q0=makeQuery(id+"F19.imprint","IMPRINT",FACE,{"disambiguationData":[TD([[makeQuery(id+"F19.imprint","IMPRINT",EDGE,{"derivedFrom":subQ0}),-1.0]])]});}
            extrude(context, id + "F20", {"entities" : qUnion([Q0]), "operationType" : NewBodyOperationType.REMOVE, "oppositeDirection" : true, "depth" : 15 * mm});
        }
    });
